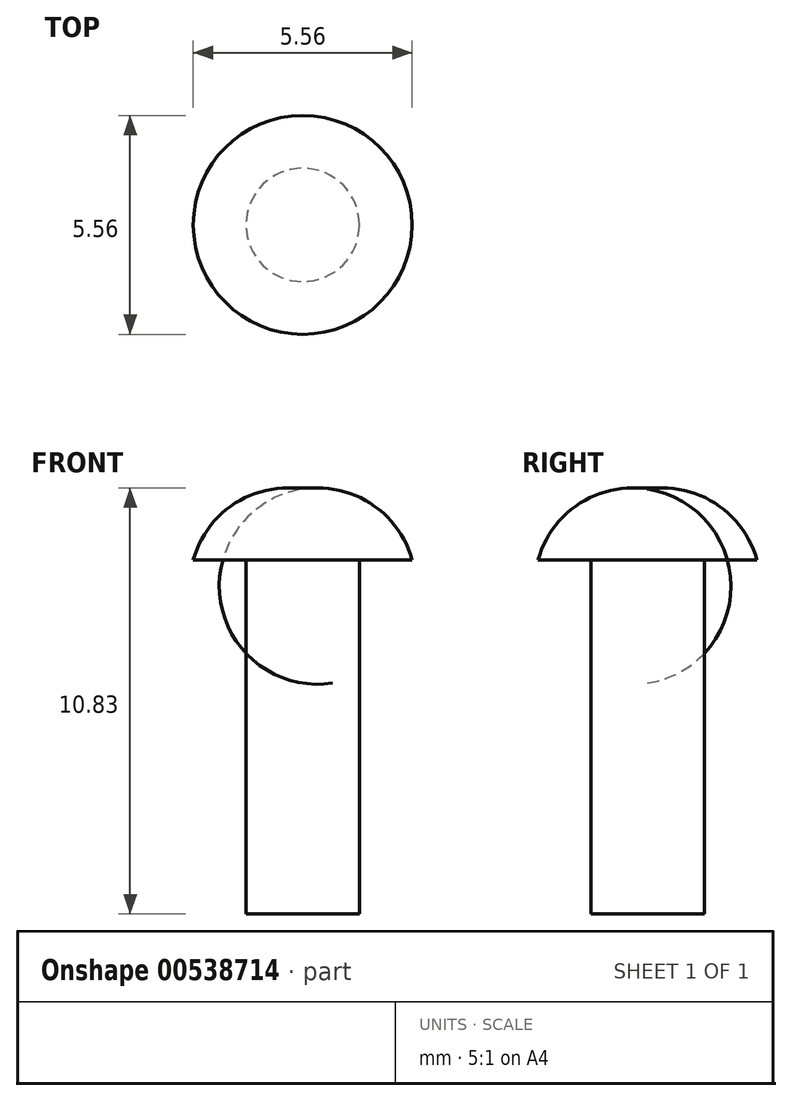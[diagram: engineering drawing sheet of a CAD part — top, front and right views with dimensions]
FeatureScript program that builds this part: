
annotation { "Feature Type Name" : "Feature", "Feature Type Description" : "" }
export const myFeature = defineFeature(function(context is Context, id is Id, definition is map)
    precondition{}
    {
        {
            var Q0;
            Q0=qCreatedBy(makeId("Front.planeOp"),FACE);
            var sketch = newSketch(context, id + "F0", { "sketchPlane" : qUnion([Q0])});
            skLineSegment(sketch, "E0", {"start": v(0, -9) * mm, "end": v(1.44, -9) * mm});
            skLineSegment(sketch, "E1", {"start": v(1.44, -9) * mm, "end": v(1.44, 0) * mm});
            skLineSegment(sketch, "E2", {"start": v(1.44, 0) * mm, "end": v(2.78, 0) * mm});
            skArc(sketch, "E3", {"start": v(2.78, 0) * mm, "mid": v(1.73, 1.43) * mm, "end": v(0, 1.8) * mm});
            skPoint(sketch, "E3.second.point", {"position": v(1.35, 1.63) * mm});
            skPoint(sketch, "E3.third.point", {"position": v(2.62, 0.42) * mm});
            skLineSegment(sketch, "E4", {"start": v(0, 1.8) * mm, "end": v(0, -9) * mm});
            skPoint(sketch, "E5.orphan", {"position": v(0, 2.86) * mm});
            skSolve(sketch);
        }
        {
            var Q0;
            Q0=makeQuery(id+"F0.imprint","IMPRINT",FACE,{"disambiguationData":[TD([[makeQuery(id+"F0.imprint","IMPRINT",EDGE,{"derivedFrom":sQuery(id+"F0.wireOp",EDGE,"E0")}),1.0]])]});
            var Q1;
            Q1=sQuery(id+"F0.wireOp",EDGE,"E4");
            revolve(context, id + "F1", {"entities" : qUnion([Q0]), "axis" : qUnion([Q1]), "revolveType" : RevolveType.FULL});
        }
    });
